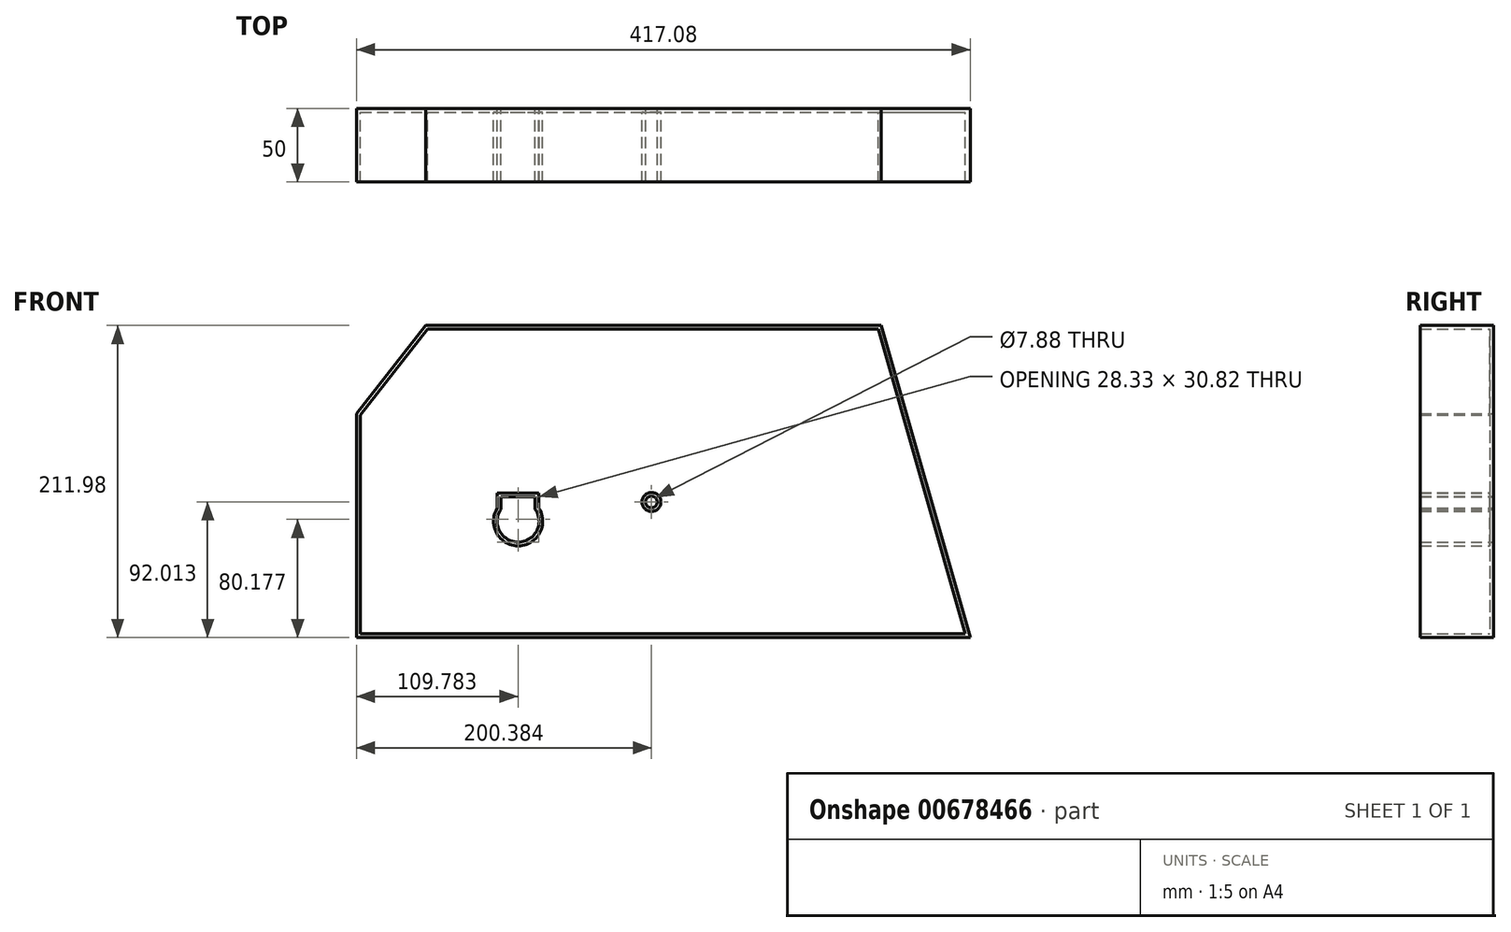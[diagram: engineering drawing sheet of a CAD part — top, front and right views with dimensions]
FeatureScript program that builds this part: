
annotation { "Feature Type Name" : "Feature", "Feature Type Description" : "" }
export const myFeature = defineFeature(function(context is Context, id is Id, definition is map)
    precondition{}
    {
        {
            var Q0;
            Q0=qCreatedBy(makeId("Front.planeOp"),FACE);
            var sketch = newSketch(context, id + "F0", { "sketchPlane" : qUnion([Q0])});
            skLineSegment(sketch, "E0", {"start": v(-110.71, 71.74) * mm, "end": v(-110.71, -80.19) * mm});
            skLineSegment(sketch, "E1", {"start": v(-110.71, -80.19) * mm, "end": v(306.37, -80.19) * mm});
            skLineSegment(sketch, "E2", {"start": v(-110.71, 71.74) * mm, "end": v(-63.68, 131.79) * mm});
            skLineSegment(sketch, "E3", {"start": v(-63.68, 131.79) * mm, "end": v(245.7, 131.79) * mm});
            skLineSegment(sketch, "E4", {"start": v(245.7, 131.79) * mm, "end": v(306.37, -80.19) * mm});
            skCircle(sketch, "E5", {"center": v(-0.93, -1.23) * mm, "radius": 14.2 * mm});
            skLineSegment(sketch, "E6", {"start": v(-12.6, 6.84) * mm, "end": v(-12.6, 15.4) * mm});
            skLineSegment(sketch, "E7", {"start": v(-12.6, 15.4) * mm, "end": v(10.72, 15.4) * mm});
            skLineSegment(sketch, "E8", {"start": v(10.72, 15.4) * mm, "end": v(10.72, 6.89) * mm});
            skCircle(sketch, "E9", {"center": v(89.67, 11.82) * mm, "radius": 3.94 * mm});
            skSolve(sketch);
        }
        {
            var Q0;
            Q0=makeQuery(id+"F0.imprint","IMPRINT",FACE,{"disambiguationData":[TD([[makeQuery(id+"F0.imprint","IMPRINT",EDGE,{"derivedFrom":sQuery(id+"F0.wireOp",EDGE,"E0")}),1.0]])]});
            extrude(context, id + "F1", {"entities" : qUnion([Q0]), "depth" : 50 * mm, "offsetDistance" : 25 * mm});
        }
        {
            var Q0;
            Q0=makeQuery(id+"F1.opExtrude","CAP_FACE",FACE,{"disambiguationData":[OSD([sQuery(id+"F0.wireOp",EDGE,"E0"),sQuery(id+"F0.wireOp",EDGE,"E1"),sQuery(id+"F0.wireOp",EDGE,"E2"),sQuery(id+"F0.wireOp",EDGE,"E3"),sQuery(id+"F0.wireOp",EDGE,"E4")])],"isStart":false});
            shell(context, id + "F2", {"entities" : qUnion([Q0]), "thickness" : 2.5 * mm});
        }
    });
